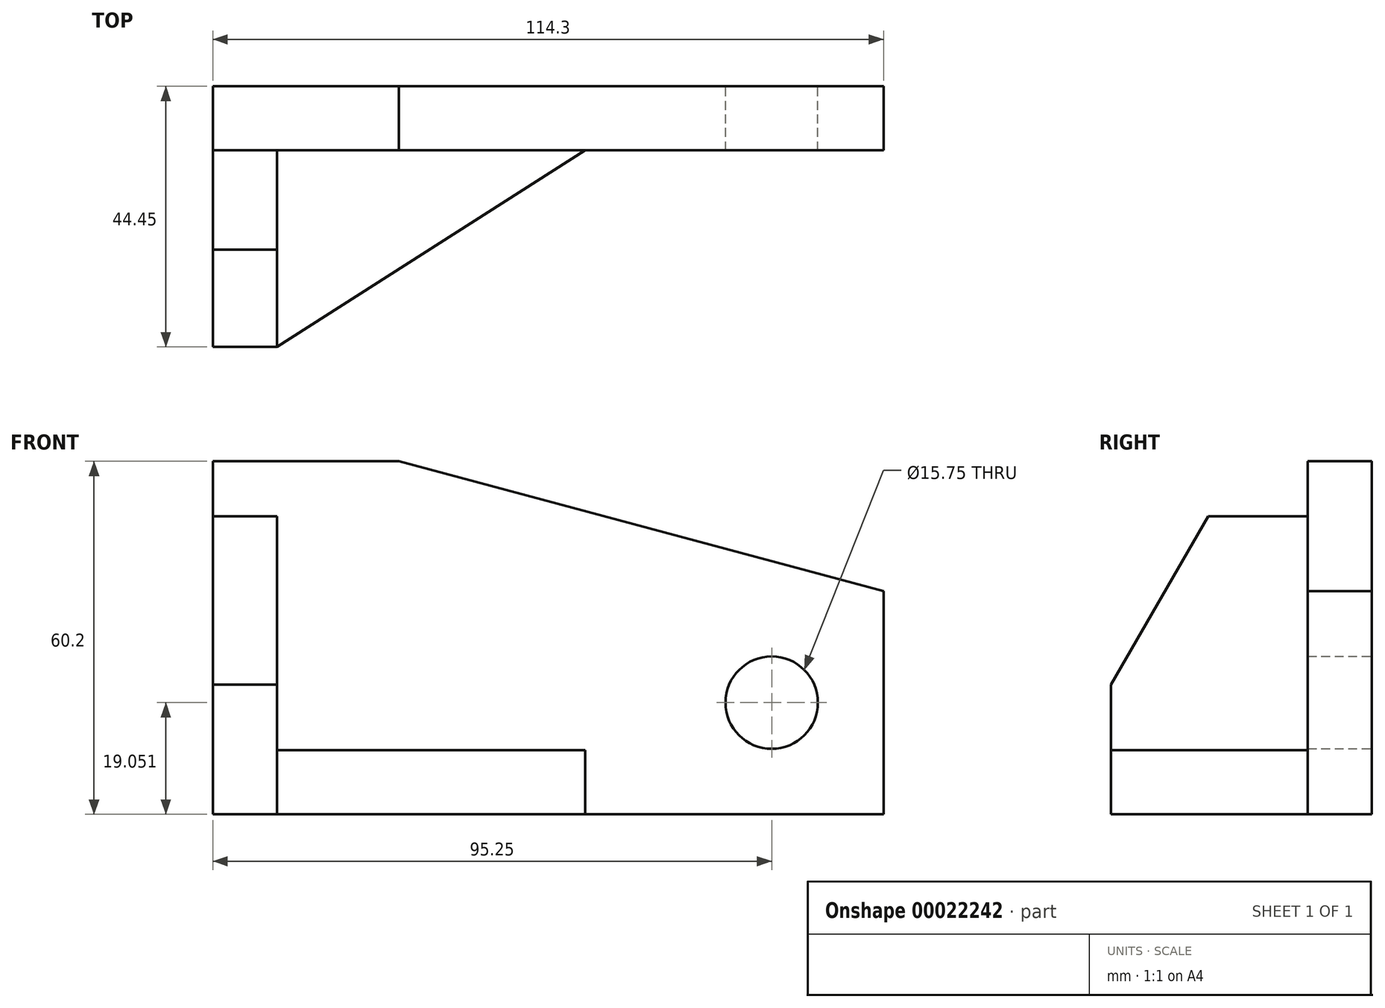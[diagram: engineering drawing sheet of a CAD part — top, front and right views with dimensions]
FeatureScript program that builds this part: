
annotation { "Feature Type Name" : "Feature", "Feature Type Description" : "" }
export const myFeature = defineFeature(function(context is Context, id is Id, definition is map)
    precondition{}
    {
        {
            var Q0;
            Q0=qCreatedBy(makeId("Front.planeOp"),FACE);
            var sketch = newSketch(context, id + "F0", { "sketchPlane" : qUnion([Q0])});
            skLineSegment(sketch, "E0.rect.bottom", {"start": v(-57.15, 30.1) * mm, "end": v(-25.4, 30.1) * mm});
            skLineSegment(sketch, "E0.rect.top", {"start": v(-57.15, -30.1) * mm, "end": v(57.15, -30.1) * mm});
            skLineSegment(sketch, "E0.rect.left", {"start": v(-57.15, 30.1) * mm, "end": v(-57.15, -30.1) * mm});
            skLineSegment(sketch, "E0.rect.right", {"start": v(57.15, 7.98) * mm, "end": v(57.15, -30.1) * mm});
            skPoint(sketch, "E0.rect.middle", {"position": v(0, 0) * mm});
            skLineSegment(sketch, "E1", {"start": v(-25.4, 30.1) * mm, "end": v(57.15, 7.98) * mm});
            skLineSegment(sketch, "E2.bottom", {"start": v(57.15, -30.1) * mm, "end": v(38.1, -30.1) * mm});
            skLineSegment(sketch, "E2.left", {"start": v(57.15, -30.1) * mm, "end": v(57.15, -11.05) * mm});
            skCircle(sketch, "E3", {"center": v(38.1, -11.05) * mm, "radius": 7.87 * mm});
            skPoint(sketch, "E4.orphan", {"position": v(57.15, 30.1) * mm});
            skSolve(sketch);
        }
        {
            var Q0;
            Q0 = qSketchRegion(id + "F0", true);
            extrude(context, id + "F1", {"entities" : qUnion([Q0]), "depth" : 10.92 * mm});
        }
        {
            var Q0;
            Q0=makeQuery(id+"F1.opExtrude","SWEPT_FACE",FACE,{"disambiguationData":[OSD([sQuery(id+"F0.wireOp",EDGE,"E0.rect.left")])]});
            var sketch = newSketch(context, id + "F2", { "sketchPlane" : qUnion([Q0])});
            skLineSegment(sketch, "E5.bottom", {"start": v(10.92, -30.1) * mm, "end": v(44.45, -30.1) * mm});
            skLineSegment(sketch, "E5.top", {"start": v(10.92, 20.7) * mm, "end": v(27.88, 20.7) * mm});
            skLineSegment(sketch, "E5.left", {"start": v(10.92, -30.1) * mm, "end": v(10.92, 20.7) * mm});
            skLineSegment(sketch, "E5.right", {"start": v(44.45, -30.1) * mm, "end": v(44.45, -8) * mm});
            skLineSegment(sketch, "E6", {"start": v(27.88, 20.7) * mm, "end": v(44.45, -8) * mm});
            skSolve(sketch);
        }
        {
            var Q0;
            Q0 = qSketchRegion(id + "F2", true);
            extrude(context, id + "F3", {"entities" : qUnion([Q0]), "oppositeDirection" : true, "depth" : 10.92 * mm});
        }
        {
            var Q0;
            Q0=makeQuery(id+"F3.opExtrude","SWEPT_FACE",FACE,{"disambiguationData":[OSD([sQuery(id+"F2.wireOp",EDGE,"E5.bottom")])]});
            var sketch = newSketch(context, id + "F4", { "sketchPlane" : qUnion([Q0])});
            skLineSegment(sketch, "E7.bottom", {"start": v(-46.23, 10.92) * mm, "end": v(6.35, 10.92) * mm});
            skLineSegment(sketch, "E7.left", {"start": v(-46.23, 10.92) * mm, "end": v(-46.23, 44.45) * mm});
            skLineSegment(sketch, "E8", {"start": v(-46.23, 44.45) * mm, "end": v(6.35, 10.92) * mm});
            skSolve(sketch);
        }
        {
            var Q0;
            Q0 = qSketchRegion(id + "F4", true);
            extrude(context, id + "F5", {"entities" : qUnion([Q0]), "oppositeDirection" : true, "depth" : 10.92 * mm});
        }
    });
